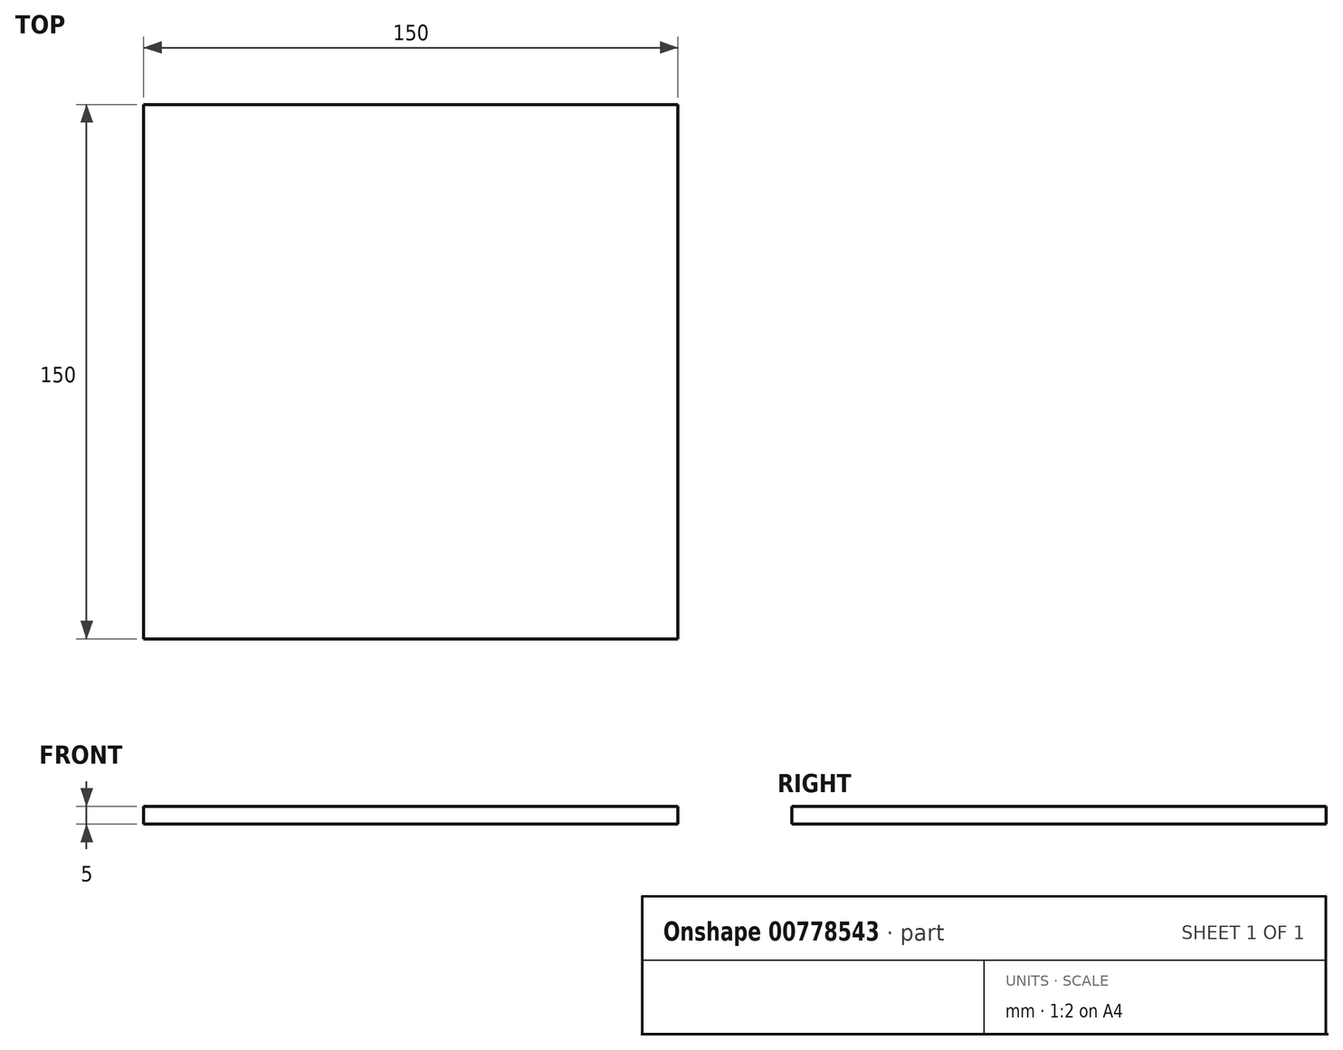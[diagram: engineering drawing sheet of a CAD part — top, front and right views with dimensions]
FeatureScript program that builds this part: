
annotation { "Feature Type Name" : "Feature", "Feature Type Description" : "" }
export const myFeature = defineFeature(function(context is Context, id is Id, definition is map)
    precondition{}
    {
        {
            var Q0;
            Q0=qCreatedBy(makeId("Top.planeOp"),FACE);
            var sketch = newSketch(context, id + "F0", { "sketchPlane" : qUnion([Q0])});
            skLineSegment(sketch, "E0.bottom", {"start": v(-74.86, 81.18) * mm, "end": v(75.14, 81.18) * mm});
            skLineSegment(sketch, "E0.top", {"start": v(-74.86, -68.82) * mm, "end": v(75.14, -68.82) * mm});
            skLineSegment(sketch, "E0.left", {"start": v(-74.86, 81.18) * mm, "end": v(-74.86, -68.82) * mm});
            skLineSegment(sketch, "E0.right", {"start": v(75.14, 81.18) * mm, "end": v(75.14, -68.82) * mm});
            skSolve(sketch);
        }
        {
            var Q0;
            Q0=makeQuery(id+"F0.imprint","IMPRINT",FACE,{"disambiguationData":[TD([[makeQuery(id+"F0.imprint","IMPRINT",EDGE,{"derivedFrom":sQuery(id+"F0.wireOp",EDGE,"E0.bottom")}),-1.0]])]});
            extrude(context, id + "F1", {"entities" : qUnion([Q0]), "depth" : 5 * mm, "offsetDistance" : 25 * mm});
        }
    });
